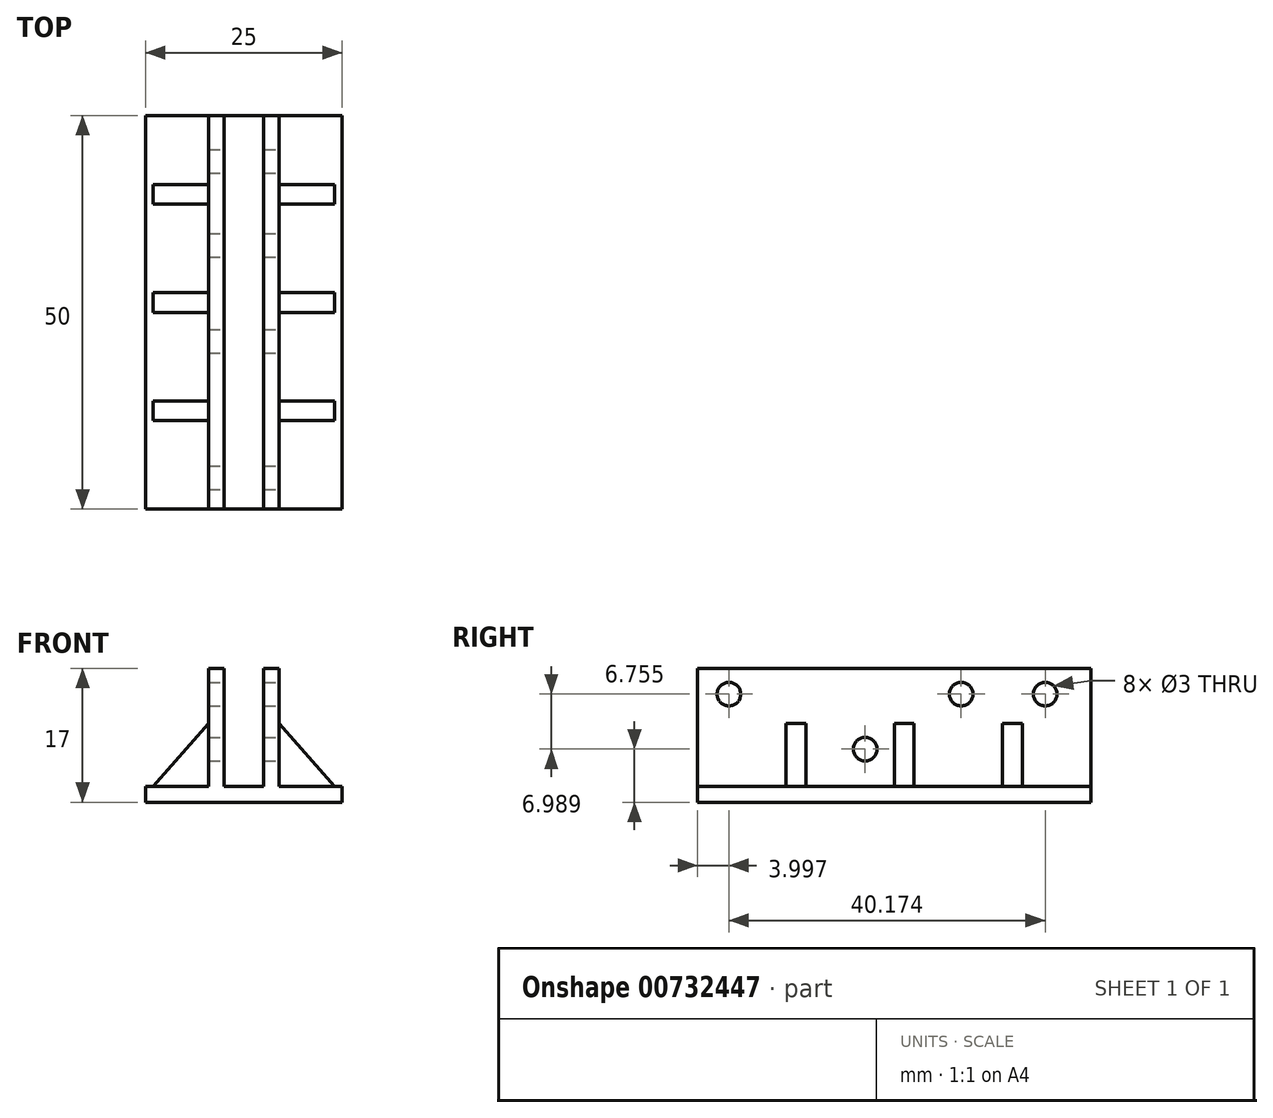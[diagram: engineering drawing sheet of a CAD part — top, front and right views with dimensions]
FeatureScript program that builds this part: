
annotation { "Feature Type Name" : "Feature", "Feature Type Description" : "" }
export const myFeature = defineFeature(function(context is Context, id is Id, definition is map)
    precondition{}
    {
        {
            var Q0;
            Q0=qCreatedBy(makeId("Front.planeOp"),FACE);
            var sketch = newSketch(context, id + "F0", { "sketchPlane" : qUnion([Q0])});
            skLineSegment(sketch, "E0.bottom", {"start": v(0, 0) * mm, "end": v(15, 0) * mm});
            skLineSegment(sketch, "E0.top", {"start": v(0, 2) * mm, "end": v(15, 2) * mm});
            skLineSegment(sketch, "E0.left", {"start": v(0, 0) * mm, "end": v(0, 2) * mm});
            skLineSegment(sketch, "E0.right", {"start": v(15, 0) * mm, "end": v(15, 2) * mm});
            skLineSegment(sketch, "E1.bottom", {"start": v(10, 2) * mm, "end": v(8, 2) * mm});
            skLineSegment(sketch, "E1.top", {"start": v(10, 17) * mm, "end": v(8, 17) * mm});
            skLineSegment(sketch, "E1.left", {"start": v(10, 2) * mm, "end": v(10, 17) * mm});
            skLineSegment(sketch, "E1.right", {"start": v(8, 2) * mm, "end": v(8, 17) * mm});
            skLineSegment(sketch, "E2", {"start": v(10, 2) * mm, "end": v(15, 0) * mm});
            skLineSegment(sketch, "E3", {"start": v(15, 2) * mm, "end": v(10, 0) * mm});
            skLineSegment(sketch, "E4", {"start": v(10, 0) * mm, "end": v(12.5, 1) * mm});
            skLineSegment(sketch, "E5", {"start": v(12.5, 1) * mm, "end": v(12.5, 3.36) * mm});
            skLineSegment(sketch, "E6.MirrorCS", {"start": v(15, 2) * mm, "end": v(15, 17) * mm});
            skLineSegment(sketch, "E7.MirrorCS", {"start": v(17, 2) * mm, "end": v(17, 17) * mm});
            skLineSegment(sketch, "E8.MirrorCS", {"start": v(15, 2) * mm, "end": v(17, 2) * mm});
            skLineSegment(sketch, "E9.MirrorCS", {"start": v(25, 0) * mm, "end": v(10, 0) * mm});
            skLineSegment(sketch, "E10.MirrorCS", {"start": v(25, 2) * mm, "end": v(10, 2) * mm});
            skLineSegment(sketch, "E11.MirrorCS", {"start": v(25, 0) * mm, "end": v(25, 2) * mm});
            skLineSegment(sketch, "E12.MirrorCS", {"start": v(15, 17) * mm, "end": v(17, 17) * mm});
            skSolve(sketch);
        }
        {
            var Q0;
            {var subQ2=sQuery(id+"F0.wireOp",EDGE,"E0.right");var subQ3=sQuery(id+"F0.wireOp",EDGE,"E0.bottom");var subQ5=sQuery(id+"F0.wireOp",EDGE,"E3");var subQ6=makeQuery(id+"F0.imprint","INTERSECT",VERTEX,{"derivedFrom":[subQ3,subQ5]});var subQ7=sQuery(id+"F0.wireOp",EDGE,"E5");var subQ10=makeQuery(id+"F0.imprint","IMPRINT",EDGE,{"disambiguationData":[TD([[subQ6,1.0]])],"derivedFrom":subQ5});var subQ13=makeQuery(id+"F0.imprint","IMPRINT",EDGE,{"derivedFrom":subQ2});var subQ14=sQuery(id+"F0.wireOp",EDGE,"E6.MirrorCS");var subQ15=sQuery(id+"F0.wireOp",EDGE,"E0.top");var subQ20=makeQuery(id+"F0.imprint","INTERSECT",VERTEX,{"derivedFrom":[subQ15,subQ7]});var subQ22=makeQuery(id+"F0.imprint","IMPRINT",EDGE,{"disambiguationData":[TD([[subQ20,1.0]])],"derivedFrom":subQ7});var subQ26=sQuery(id+"F0.wireOp",EDGE,"E0.left");Q0=qUnion([makeQuery(id+"F0.imprint","IMPRINT",FACE,{"disambiguationData":[TD([[subQ22,-1.0]])]}),makeQuery(id+"F0.imprint","IMPRINT",FACE,{"disambiguationData":[TD([[makeQuery(id+"F0.imprint","IMPRINT",EDGE,{"derivedFrom":subQ26}),-1.0]])]}),makeQuery(id+"F0.imprint","IMPRINT",FACE,{"disambiguationData":[TD([[makeQuery(id+"F0.imprint","IMPRINT",EDGE,{"derivedFrom":sQuery(id+"F0.wireOp",EDGE,"E1.top")}),1.0]])]}),makeQuery(id+"F0.imprint","IMPRINT",FACE,{"disambiguationData":[TD([[makeQuery(id+"F0.imprint","IMPRINT",EDGE,{"disambiguationData":[TD([[subQ20,1.0]])],"derivedFrom":subQ15}),-1.0]])]}),makeQuery(id+"F0.imprint","IMPRINT",FACE,{"disambiguationData":[TD([[subQ13,1.0]])]}),makeQuery(id+"F0.imprint","IMPRINT",FACE,{"disambiguationData":[TD([[makeQuery(id+"F0.imprint","IMPRINT",EDGE,{"derivedFrom":subQ14}),-1.0]])]}),makeQuery(id+"F0.imprint","IMPRINT",FACE,{"disambiguationData":[TD([[subQ13,-1.0]])]}),makeQuery(id+"F0.imprint","IMPRINT",FACE,{"disambiguationData":[TD([[subQ10,1.0]])]})]);}
            extrude(context, id + "F1", {"entities" : qUnion([Q0]), "depth" : 50 * mm, "offsetDistance" : 25 * mm});
        }
        {
            var Q0;
            Q0=makeQuery(id+"F1.opExtrude","SWEPT_FACE",FACE,{"disambiguationData":[OSD([sQuery(id+"F0.wireOp",EDGE,"E10.MirrorCS")])]});
            var sketch = newSketch(context, id + "F2", { "sketchPlane" : qUnion([Q0])});
            skLineSegment(sketch, "E13", {"start": v(25, -25) * mm, "end": v(17, -25) * mm});
            skLineSegment(sketch, "E14.top", {"start": v(25, -22.5) * mm, "end": v(17, -22.5) * mm});
            skLineSegment(sketch, "E14.left", {"start": v(25, -25) * mm, "end": v(25, -22.5) * mm});
            skLineSegment(sketch, "E14.right", {"start": v(17, -25) * mm, "end": v(17, -22.5) * mm});
            skLineSegment(sketch, "E15", {"start": v(17, -22.5) * mm, "end": v(17, -25) * mm});
            skLineSegment(sketch, "E16", {"start": v(21, -11.25) * mm, "end": v(29.84, -11.25) * mm});
            skLineSegment(sketch, "E17", {"start": v(25, -11.25) * mm, "end": v(25, -22.5) * mm});
            skLineSegment(sketch, "E18", {"start": v(25, -16.88) * mm, "end": v(23, -16.88) * mm});
            skLineSegment(sketch, "E19.MirrorCS", {"start": v(25, -11.25) * mm, "end": v(17, -11.25) * mm});
            skLineSegment(sketch, "E20.MirrorCS", {"start": v(25, -8.75) * mm, "end": v(17, -8.75) * mm});
            skLineSegment(sketch, "E21.MirrorCS", {"start": v(17, -11.25) * mm, "end": v(17, -8.75) * mm});
            skLineSegment(sketch, "E22.MirrorCS", {"start": v(25, -8.75) * mm, "end": v(25, -11.25) * mm});
            skLineSegment(sketch, "E23", {"start": v(25, -23.75) * mm, "end": v(22.95, -23.75) * mm});
            skLineSegment(sketch, "E24.MirrorCS", {"start": v(21, -36.25) * mm, "end": v(29.84, -36.25) * mm});
            skLineSegment(sketch, "E25.MirrorCS", {"start": v(25, -36.25) * mm, "end": v(17, -36.25) * mm});
            skLineSegment(sketch, "E26.MirrorCS", {"start": v(17, -36.25) * mm, "end": v(17, -38.75) * mm});
            skLineSegment(sketch, "E27.MirrorCS", {"start": v(25, -38.75) * mm, "end": v(25, -36.25) * mm});
            skLineSegment(sketch, "E28.MirrorCS", {"start": v(25, -38.75) * mm, "end": v(17, -38.75) * mm});
            skLineSegment(sketch, "E29", {"start": v(0, 0) * mm, "end": v(25, 0) * mm});
            skLineSegment(sketch, "E30", {"start": v(25, 0) * mm, "end": v(12.5, 0) * mm});
            skLineSegment(sketch, "E31", {"start": v(12.5, 0) * mm, "end": v(12.5, -11.3) * mm});
            skLineSegment(sketch, "E32.MirrorCS", {"start": v(8, -25) * mm, "end": v(8, -22.5) * mm});
            skLineSegment(sketch, "E33.MirrorCS", {"start": v(0, -25) * mm, "end": v(0, -22.5) * mm});
            skLineSegment(sketch, "E34.MirrorCS", {"start": v(0, -25) * mm, "end": v(8, -25) * mm});
            skLineSegment(sketch, "E35.MirrorCS", {"start": v(8, -22.5) * mm, "end": v(8, -25) * mm});
            skLineSegment(sketch, "E36.MirrorCS", {"start": v(0, -16.88) * mm, "end": v(2, -16.88) * mm});
            skLineSegment(sketch, "E37.MirrorCS", {"start": v(0, -22.5) * mm, "end": v(8, -22.5) * mm});
            skLineSegment(sketch, "E38.MirrorCS", {"start": v(0, -23.75) * mm, "end": v(2.05, -23.75) * mm});
            skLineSegment(sketch, "E39.MirrorCS", {"start": v(0, -38.75) * mm, "end": v(0, -36.25) * mm});
            skLineSegment(sketch, "E40.MirrorCS", {"start": v(4, -36.25) * mm, "end": v(-4.84, -36.25) * mm});
            skLineSegment(sketch, "E41.MirrorCS", {"start": v(0, -36.25) * mm, "end": v(8, -36.25) * mm});
            skLineSegment(sketch, "E42.MirrorCS", {"start": v(0, -38.75) * mm, "end": v(8, -38.75) * mm});
            skLineSegment(sketch, "E43.MirrorCS", {"start": v(8, -36.25) * mm, "end": v(8, -38.75) * mm});
            skLineSegment(sketch, "E44.MirrorCS", {"start": v(0, -11.25) * mm, "end": v(8, -11.25) * mm});
            skLineSegment(sketch, "E45.MirrorCS", {"start": v(0, -8.75) * mm, "end": v(8, -8.75) * mm});
            skLineSegment(sketch, "E46", {"start": v(0, -8.75) * mm, "end": v(0, -11.25) * mm});
            skLineSegment(sketch, "E47", {"start": v(8, -8.75) * mm, "end": v(8, -11.25) * mm});
            skSolve(sketch);
        }
        {
            var Q0;
            Q0 = qSketchRegion(id + "F2", true);
            var Q1;
            Q1=makeQuery(id+"F1.opExtrude","SWEPT_FACE",FACE,{"disambiguationData":[OSD([sQuery(id+"F0.wireOp",EDGE,"E1.top")])]});
            extrude(context, id + "F3", {"entities" : qUnion([Q0]), "operationType" : NewBodyOperationType.ADD, "endBound" : BoundingType.UP_TO_SURFACE, "depth" : 25 * mm, "endBoundEntityFace" : qUnion([Q1]), "offsetDistance" : 25 * mm});
        }
        {
            var Q0;
            Q0=makeQuery(id+"F3.opExtrude","SWEPT_FACE",FACE,{"disambiguationData":[OSD([sQuery(id+"F2.wireOp",EDGE,"E42.MirrorCS")])]});
            var sketch = newSketch(context, id + "F4", { "sketchPlane" : qUnion([Q0])});
            skLineSegment(sketch, "E48", {"start": v(0, 2) * mm, "end": v(1, 2) * mm});
            skLineSegment(sketch, "E49", {"start": v(1, 2) * mm, "end": v(8, 10) * mm});
            skSolve(sketch);
        }
        {
            var Q0;
            Q0 = qSketchRegion(id + "F4", true);
            var Q1;
            Q1=makeQuery(id+"F4.imprint","IMPRINT",FACE,{"disambiguationData":[TD([[makeQuery(id+"F4.imprint","IMPRINT",EDGE,{"derivedFrom":sQuery(id+"F4.wireOp",EDGE,"E48")}),1.0]])]});
            extrude(context, id + "F5", {"entities" : qUnion([Q0, Q1]), "operationType" : NewBodyOperationType.REMOVE, "oppositeDirection" : true, "depth" : 100 * mm, "offsetDistance" : 25 * mm});
        }
        {
            var Q0;
            Q0=makeQuery(id+"F3.opExtrude","SWEPT_FACE",FACE,{"disambiguationData":[OSD([sQuery(id+"F2.wireOp",EDGE,"E28.MirrorCS")])]});
            var sketch = newSketch(context, id + "F6", { "sketchPlane" : qUnion([Q0])});
            skLineSegment(sketch, "E50", {"start": v(24, 2) * mm, "end": v(17, 10) * mm});
            skSolve(sketch);
        }
        {
            var Q0;
            Q0 = qSketchRegion(id + "F6", true);
            var Q1;
            {var subQ4=sQuery(id+"F6.wireOp",EDGE,"E50");Q1=makeQuery(id+"F6.imprint","IMPRINT",FACE,{"disambiguationData":[TD([[makeQuery(id+"F6.imprint","IMPRINT",EDGE,{"derivedFrom":subQ4}),-1.0]])]});}
            extrude(context, id + "F7", {"entities" : qUnion([Q0, Q1]), "operationType" : NewBodyOperationType.REMOVE, "oppositeDirection" : true, "depth" : 34.4 * mm, "offsetDistance" : 25 * mm});
        }
        {
            var Q0;
            {var subQ0=sQuery(id+"F2.wireOp",EDGE,"E28.MirrorCS");var subQ1=sQuery(id+"F2.wireOp",EDGE,"E26.MirrorCS");var subQ2=sQuery(id+"F0.wireOp",EDGE,"E10.MirrorCS");var subQ3=sQuery(id+"F0.wireOp",EDGE,"E7.MirrorCS");var subQ4=sQuery(id+"F2.wireOp",EDGE,"E14.top");var subQ5=sQuery(id+"F2.wireOp",EDGE,"E13");var subQ13=sQuery(id+"F2.wireOp",EDGE,"E20.MirrorCS");var subQ15=makeQuery(id+"F1.opExtrude","SWEPT_FACE",FACE,{"disambiguationData":[OSD([subQ3])]});Q0=makeQuery(id+"F7.boolean.opBoolean","MERGE",FACE,{"derivedFrom":[makeQuery(id+"F3.boolean.opBoolean","SPLIT",FACE,{"disambiguationData":[TD([makeQuery(id+"F3.opExtrude","SWEPT_FACE",FACE,{"disambiguationData":[OSD([subQ13])]})])],"derivedFrom":subQ15}),makeQuery(id+"F3.boolean.opBoolean","SPLIT",FACE,{"disambiguationData":[TD([makeQuery(id+"F3.opExtrude","SWEPT_FACE",FACE,{"disambiguationData":[OSD([subQ0])]})])],"derivedFrom":subQ15}),makeQuery(id+"F3.boolean.opBoolean","SPLIT",FACE,{"disambiguationData":[TD([makeQuery(id+"F3.opExtrude","SWEPT_FACE",FACE,{"disambiguationData":[OSD([subQ5])]})])],"derivedFrom":subQ15}),makeQuery(id+"F3.boolean.opBoolean","SPLIT",FACE,{"disambiguationData":[TD([makeQuery(id+"F3.opExtrude","SWEPT_FACE",FACE,{"disambiguationData":[OSD([subQ4])]})])],"derivedFrom":subQ15})],"fromTools":[makeQuery(id+"F7.opExtrude","SWEPT_FACE",FACE,{"disambiguationData":[OSD([subQ3,sQuery(id+"F0.wireOp",EDGE,"E8.MirrorCS"),subQ2,subQ1,subQ0])]})]});}
            var sketch = newSketch(context, id + "F8", { "sketchPlane" : qUnion([Q0])});
            skCircle(sketch, "E51", {"center": v(-46, 13.74) * mm, "radius": 1.5 * mm});
            skCircle(sketch, "E52", {"center": v(-28.7, 6.75) * mm, "radius": 1.5 * mm});
            skLineSegment(sketch, "E53", {"start": v(-46, 13.74) * mm, "end": v(-50, 13.74) * mm});
            skLineSegment(sketch, "E54", {"start": v(-50, 13.74) * mm, "end": v(-16.5, 13.74) * mm});
            skLineSegment(sketch, "E55", {"start": v(-16.5, 13.74) * mm, "end": v(0, 13.74) * mm});
            skCircle(sketch, "E56", {"center": v(-16.5, 13.74) * mm, "radius": 1.5 * mm});
            skCircle(sketch, "E57", {"center": v(-5.83, 13.74) * mm, "radius": 1.5 * mm});
            skSolve(sketch);
        }
        {
            var Q0;
            Q0 = qSketchRegion(id + "F8", true);
            var Q1;
            {var subQ0=sQuery(id+"F2.wireOp",EDGE,"E43.MirrorCS");var subQ1=sQuery(id+"F2.wireOp",EDGE,"E42.MirrorCS");var subQ2=sQuery(id+"F2.wireOp",EDGE,"E34.MirrorCS");var subQ6=sQuery(id+"F2.wireOp",EDGE,"E37.MirrorCS");var subQ10=sQuery(id+"F0.wireOp",EDGE,"E1.right");var subQ13=sQuery(id+"F2.wireOp",EDGE,"E45.MirrorCS");var subQ16=makeQuery(id+"F1.opExtrude","SWEPT_FACE",FACE,{"disambiguationData":[OSD([subQ10])]});Q1=makeQuery(id+"F5.boolean.opBoolean","MERGE",FACE,{"derivedFrom":[makeQuery(id+"F3.boolean.opBoolean","SPLIT",FACE,{"disambiguationData":[TD([makeQuery(id+"F3.opExtrude","SWEPT_FACE",FACE,{"disambiguationData":[OSD([subQ13])]})])],"derivedFrom":subQ16}),makeQuery(id+"F3.boolean.opBoolean","SPLIT",FACE,{"disambiguationData":[TD([makeQuery(id+"F3.opExtrude","SWEPT_FACE",FACE,{"disambiguationData":[OSD([subQ1])]})])],"derivedFrom":subQ16}),makeQuery(id+"F3.boolean.opBoolean","SPLIT",FACE,{"disambiguationData":[TD([makeQuery(id+"F3.opExtrude","SWEPT_FACE",FACE,{"disambiguationData":[OSD([subQ6])]})])],"derivedFrom":subQ16}),makeQuery(id+"F3.boolean.opBoolean","SPLIT",FACE,{"disambiguationData":[TD([makeQuery(id+"F3.opExtrude","SWEPT_FACE",FACE,{"disambiguationData":[OSD([subQ2])]})])],"derivedFrom":subQ16})],"fromTools":[makeQuery(id+"F5.opExtrude","SWEPT_FACE",FACE,{"disambiguationData":[OSD([subQ1,subQ0])]})]});}
            extrude(context, id + "F9", {"entities" : qUnion([Q0]), "operationType" : NewBodyOperationType.REMOVE, "endBound" : BoundingType.UP_TO_SURFACE, "oppositeDirection" : true, "depth" : 25 * mm, "endBoundEntityFace" : qUnion([Q1]), "offsetDistance" : 25 * mm});
        }
    });
